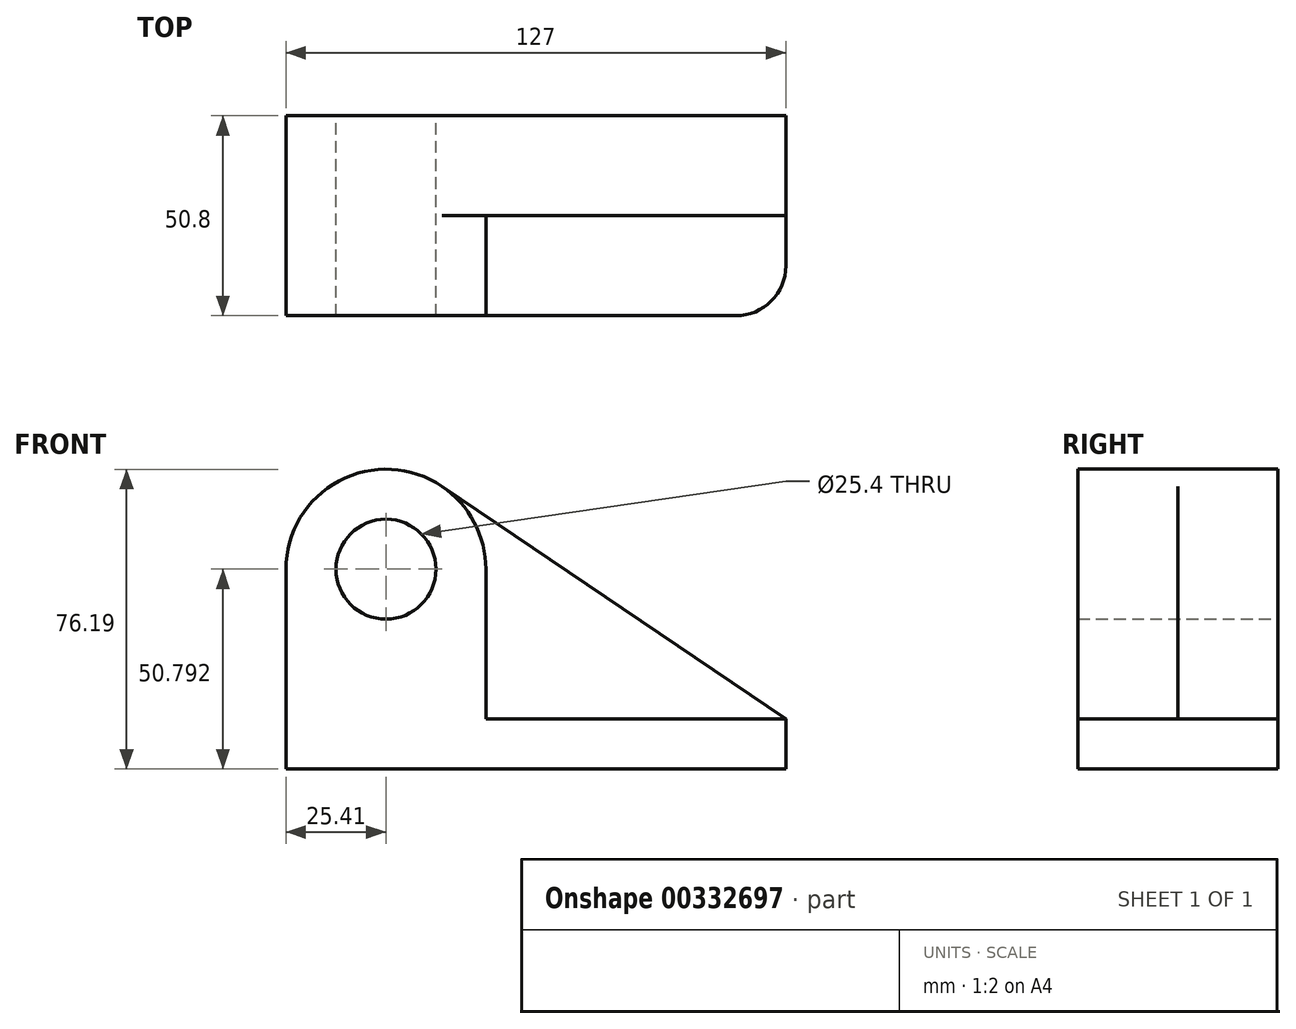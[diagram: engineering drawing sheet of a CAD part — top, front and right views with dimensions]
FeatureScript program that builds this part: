
annotation { "Feature Type Name" : "Feature", "Feature Type Description" : "" }
export const myFeature = defineFeature(function(context is Context, id is Id, definition is map)
    precondition{}
    {
        {
            var Q0;
            Q0=qCreatedBy(makeId("Front.planeOp"),FACE);
            var sketch = newSketch(context, id + "F0", { "sketchPlane" : qUnion([Q0])});
            skCircle(sketch, "E0", {"center": v(-46.35, 31.88) * mm, "radius": 12.7 * mm});
            skArc(sketch, "E1", {"start": v(-32.11, 52.92) * mm, "mid": v(-58.25, 54.32) * mm, "end": v(-71.75, 31.89) * mm});
            skLineSegment(sketch, "E2", {"start": v(-71.75, 31.89) * mm, "end": v(-71.76, -18.91) * mm});
            skLineSegment(sketch, "E3", {"start": v(-71.76, -18.91) * mm, "end": v(55.24, -18.91) * mm});
            skLineSegment(sketch, "E4", {"start": v(55.24, -18.91) * mm, "end": v(55.24, -6.21) * mm});
            skLineSegment(sketch, "E5", {"start": v(55.24, -6.21) * mm, "end": v(-32.11, 52.92) * mm});
            skSolve(sketch);
        }
        {
            var Q0;
            Q0=makeQuery(id+"F0.imprint","IMPRINT",FACE,{"disambiguationData":[TD([[makeQuery(id+"F0.imprint","IMPRINT",EDGE,{"derivedFrom":sQuery(id+"F0.wireOp",EDGE,"E0")}),-1.0]])]});
            extrude(context, id + "F1", {"entities" : qUnion([Q0]), "depth" : 25.4 * mm});
        }
        {
            var Q0;
            Q0=makeQuery(id+"F1.opExtrude","CAP_FACE",FACE,{"disambiguationData":[OSD([sQuery(id+"F0.wireOp",EDGE,"E0"),sQuery(id+"F0.wireOp",EDGE,"E1"),sQuery(id+"F0.wireOp",EDGE,"E2"),sQuery(id+"F0.wireOp",EDGE,"E3"),sQuery(id+"F0.wireOp",EDGE,"E4"),sQuery(id+"F0.wireOp",EDGE,"E5")])],"isStart":false});
            var sketch = newSketch(context, id + "F2", { "sketchPlane" : qUnion([Q0])});
            skCircle(sketch, "E6", {"center": v(-46.35, 31.88) * mm, "radius": 12.7 * mm});
            skArc(sketch, "E7", {"start": v(-20.95, 31.88) * mm, "mid": v(-46.35, 57.28) * mm, "end": v(-71.75, 31.89) * mm});
            skLineSegment(sketch, "E8.bottom", {"start": v(55.24, -6.21) * mm, "end": v(-20.95, -6.21) * mm});
            skLineSegment(sketch, "E8.top", {"start": v(55.24, -18.91) * mm, "end": v(-71.76, -18.91) * mm});
            skLineSegment(sketch, "E8.left", {"start": v(55.24, -6.21) * mm, "end": v(55.24, -18.91) * mm});
            skLineSegment(sketch, "E8.right", {"start": v(-71.76, -6.21) * mm, "end": v(-71.76, -18.91) * mm});
            skLineSegment(sketch, "E9", {"start": v(-20.95, 31.88) * mm, "end": v(-20.95, -6.21) * mm});
            skLineSegment(sketch, "E10", {"start": v(-71.75, 31.89) * mm, "end": v(-71.76, -12.56) * mm});
            skPoint(sketch, "E10.endSnap0", {"position": v(-71.76, -12.56) * mm});
            skLineSegment(sketch, "E11.trimOffspring", {"start": v(-71.76, -6.21) * mm, "end": v(-71.76, -6.21) * mm});
            skSolve(sketch);
        }
        {
            var Q0;
            Q0=makeQuery(id+"F2.imprint","IMPRINT",FACE,{"disambiguationData":[TD([[makeQuery(id+"F2.imprint","IMPRINT",EDGE,{"derivedFrom":sQuery(id+"F2.wireOp",EDGE,"E6")}),-1.0]])]});
            extrude(context, id + "F3", {"entities" : qUnion([Q0]), "operationType" : NewBodyOperationType.ADD, "depth" : 25.4 * mm});
        }
        {
            var Q0;
            Q0=makeQuery(id+"F3.opExtrude","CAP_EDGE",EDGE,{"disambiguationData":[OSD([sQuery(id+"F2.wireOp",EDGE,"E8.left")])],"isStart":false});
            fillet(context, id + "F4", {"entities" : qUnion([Q0]), "radius" : 12.7 * mm, "tangentPropagation" : true, "allowEdgeOverflow" : false});
        }
    });
